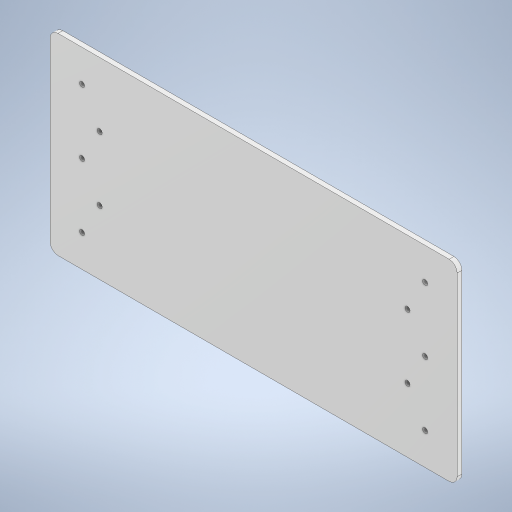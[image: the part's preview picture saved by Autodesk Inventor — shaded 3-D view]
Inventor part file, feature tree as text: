
AUTODESK INVENTOR PART (.ipt)
format: ipt  version: 2024.3 (Build 283343000, 343)  size: 274,432 bytes
history: native  units: mm
features: sketch x4, extrude x3, other x1, fillet x1, hole x1
ambient origin geometry x8: Origin, YZ Plane, XZ Plane, XY Plane, X Axis, Y Axis, Z Axis, Center Point
bodies: Body1 (feature_tree)
feature tree (10):
  other  "ソリッド1"
  extrude  "押し出し1"  Depth=260.0mm
  extrude  "押し出し4"  Depth=3.0mm
  extrude  "押し出し7"  Depth=120.0mm TaperAngle=0.0deg
  fillet  "フィレット1"  Radius=3.0mm
  hole  "穴1"  [1 undecoded]
  sketch  "スケッチ1"
  sketch  "スケッチ5"
  sketch  "スケッチ8"
  sketch  "スケッチ13"
note: 1 required parameter value undecoded (feature->parameter linkage not recoverable at this tier; creation-order binding heuristic only, values carry confidence <= 0.55)
